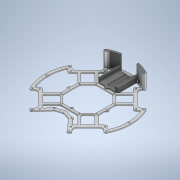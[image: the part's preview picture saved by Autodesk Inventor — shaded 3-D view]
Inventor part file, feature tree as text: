
AUTODESK INVENTOR PART (.ipt)
format: ipt  version: 2020 (Build 240168000, 168)  size: 1,823,232 bytes
history: native  units: mm
features: projected_geometry x33, extrude x18, sketch x12, other x4, fillet x3, chamfer x1
ambient origin geometry x8: Origin, YZ Plane, XZ Plane, XY Plane, X Axis, Y Axis, Z Axis, Center Point
bodies: Body1 (feature_tree)
feature tree (71):
  other  "Твердое тело1"
  extrude  "outer"  TaperAngle=45.0deg  [1 undecoded]
  extrude  "inner"  Depth=7.0mm
  sketch  "Эскиз3"
  extrude  "Выдавливание3"  Depth=20.0mm
  extrude  "Выдавливание4"  Depth=7.0mm
  sketch  "Эскиз4"
  extrude  "Выдавливание5"  Depth=3.2mm
  extrude  "Выдавливание6"  Depth=59.0mm
  sketch  "Эскиз5"
  extrude  "Выдавливание7"  Depth=83.0mm
  extrude  "Выдавливание8"  Depth=69.0mm
  sketch  "Эскиз6"
  extrude  "Выдавливание9"  Depth=55.0mm
  extrude  "Выдавливание10"  Depth=3.0mm
  other  "РабПлоскость1"
  extrude  "Выдавливание11"  Depth=8.0mm
  chamfer  "Фаска1"  Distance=5.0mm
  fillet  "Сопряжение1"  Radius=2.0mm
  fillet  "Сопряжение2"  Radius=40.0mm
  other  "РабПлоскость2"
  extrude  "Выдавливание12"  Depth=2.0mm
  sketch  "Эскиз9"
  extrude  "Выдавливание13"  Depth=105.0mm
  extrude  "Выдавливание14"  Depth=2.0mm
  other  "РабПлоскость3"
  extrude  "Выдавливание15"  Depth=2.0mm TaperAngle=0.0deg
  extrude  "Выдавливание16"  Depth=3.5mm
  fillet  "Сопряжение3"  Radius=2.0mm
  extrude  "Выдавливание17"  Depth=6.0mm
  extrude  "Выдавливание18"  Depth=12.0mm
  sketch  "Эскиз1"
  sketch  "Эскиз2"
  projected_geometry  "Спроецированная петля1"
  projected_geometry  "Спроецированная петля2"
  projected_geometry  "Спроецированная петля3"
  projected_geometry  "Спроецированная петля4"
  projected_geometry  "Спроецированная петля5"
  sketch  "Эскиз7"
  projected_geometry  "Спроецированная петля6"
  projected_geometry  "Спроецированная петля7"
  projected_geometry  "Спроецированная петля8"
  sketch  "Эскиз8"
  projected_geometry  "Спроецированная петля9"
  projected_geometry  "Спроецированная петля10"
  projected_geometry  "Спроецированная петля11"
  projected_geometry  "Спроецированная петля12"
  projected_geometry  "Спроецированная петля13"
  projected_geometry  "Спроецированная петля14"
  projected_geometry  "Спроецированная петля15"
  sketch  "Эскиз10"
  projected_geometry  "Спроецированная петля16"
  projected_geometry  "Спроецированная петля17"
  projected_geometry  "Спроецированная петля18"
  projected_geometry  "Спроецированная петля19"
  projected_geometry  "Спроецированная петля20"
  projected_geometry  "Спроецированная петля21"
  projected_geometry  "Спроецированная петля22"
  projected_geometry  "Спроецированная петля23"
  projected_geometry  "Спроецированная петля24"
  projected_geometry  "Спроецированная петля25"
  sketch  "Эскиз11"
  sketch  "Эскиз12"
  projected_geometry  "Спроецированная петля26"
  projected_geometry  "Спроецированная петля27"
  projected_geometry  "Спроецированная петля28"
  projected_geometry  "Спроецированная петля29"
  projected_geometry  "Спроецированная петля30"
  projected_geometry  "Спроецированная петля31"
  projected_geometry  "Спроецированная петля32"
  projected_geometry  "Спроецированная петля33"
note: 1 required parameter value undecoded (feature->parameter linkage not recoverable at this tier; creation-order binding heuristic only, values carry confidence <= 0.55)
